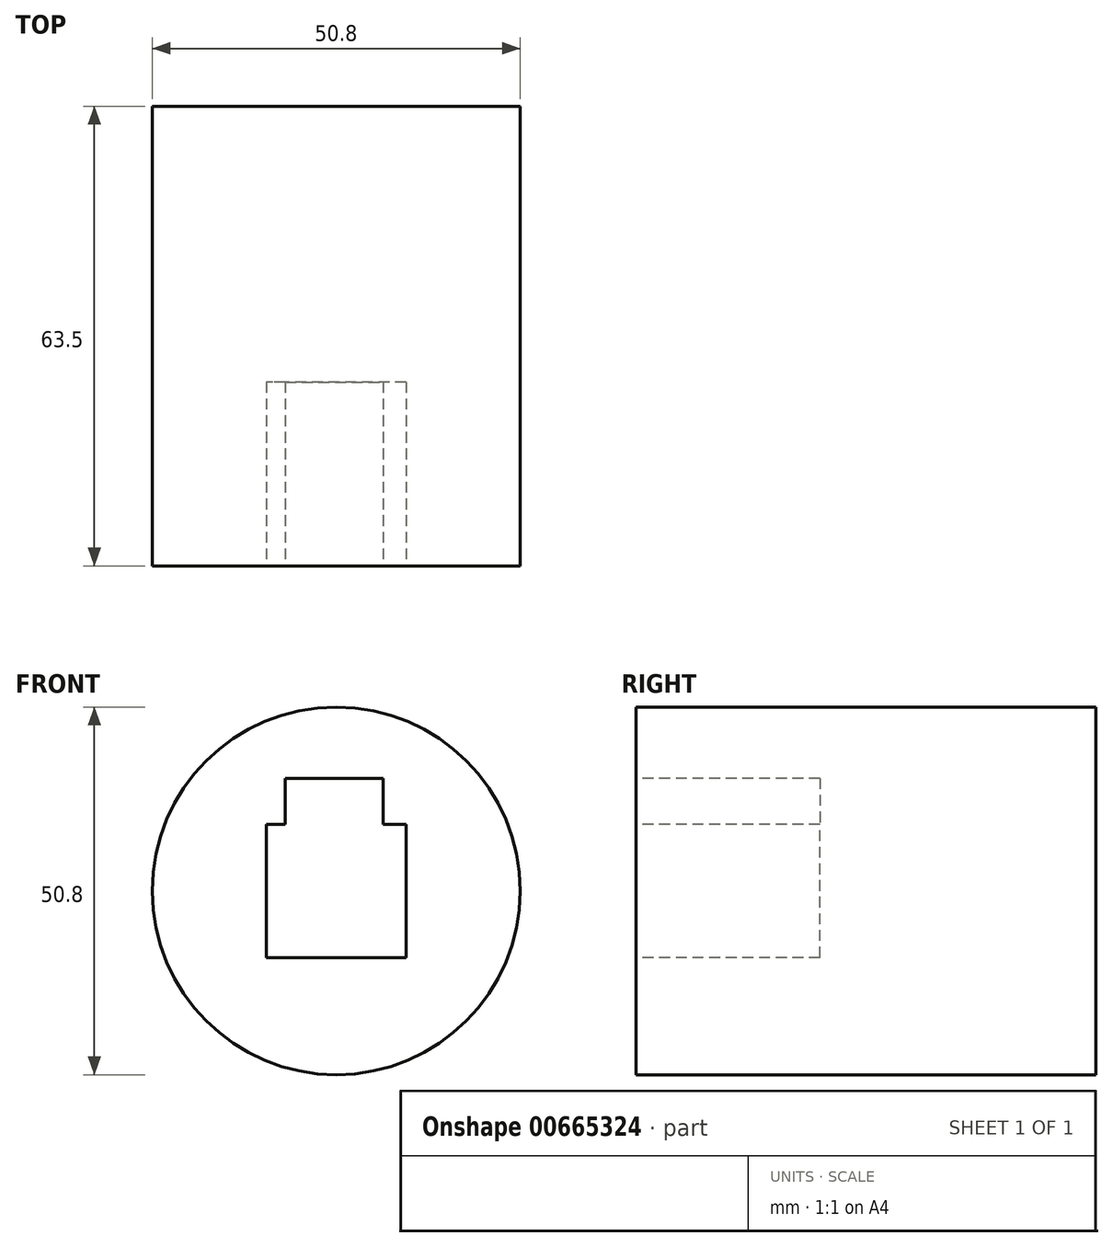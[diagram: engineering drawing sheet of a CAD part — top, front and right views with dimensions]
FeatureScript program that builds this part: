
annotation { "Feature Type Name" : "Feature", "Feature Type Description" : "" }
export const myFeature = defineFeature(function(context is Context, id is Id, definition is map)
    precondition{}
    {
        {
            var Q0;
            Q0=qCreatedBy(makeId("Front.planeOp"),FACE);
            var sketch = newSketch(context, id + "F0", { "sketchPlane" : qUnion([Q0])});
            skCircle(sketch, "E0", {"center": v(0, 0) * mm, "radius": 25.4 * mm});
            skSolve(sketch);
        }
        {
            var Q0;
            Q0 = qSketchRegion(id + "F0", true);
            extrude(context, id + "F1", {"entities" : qUnion([Q0]), "depth" : 63.5 * mm, "offsetDistance" : 25.4 * mm});
        }
        {
            var Q0;
            Q0=makeQuery(id+"F1.opExtrude","CAP_FACE",FACE,{"disambiguationData":[OSD([sQuery(id+"F0.wireOp",EDGE,"E0")])],"isStart":false});
            var sketch = newSketch(context, id + "F2", { "sketchPlane" : qUnion([Q0])});
            skLineSegment(sketch, "E1.bottom", {"start": v(9.64, -9.21) * mm, "end": v(-9.64, -9.21) * mm});
            skLineSegment(sketch, "E1.top", {"start": v(9.64, 9.21) * mm, "end": v(-9.64, 9.21) * mm});
            skLineSegment(sketch, "E1.left", {"start": v(9.64, -9.21) * mm, "end": v(9.64, 9.21) * mm});
            skLineSegment(sketch, "E1.right", {"start": v(-9.64, -9.21) * mm, "end": v(-9.64, 9.21) * mm});
            skPoint(sketch, "E1.middle", {"position": v(0, 0) * mm});
            skSolve(sketch);
        }
        {
            var Q0;
            Q0 = qSketchRegion(id + "F2", true);
            extrude(context, id + "F3", {"entities" : qUnion([Q0]), "operationType" : NewBodyOperationType.REMOVE, "oppositeDirection" : true, "depth" : 25.4 * mm, "offsetDistance" : 25.4 * mm});
        }
        {
            var Q0;
            Q0=makeQuery(id+"F1.opExtrude","CAP_FACE",FACE,{"disambiguationData":[OSD([sQuery(id+"F0.wireOp",EDGE,"E0")])],"isStart":false});
            var sketch = newSketch(context, id + "F4", { "sketchPlane" : qUnion([Q0])});
            skLineSegment(sketch, "E2.bottom", {"start": v(-7.05, 15.56) * mm, "end": v(6.46, 15.56) * mm});
            skLineSegment(sketch, "E2.top", {"start": v(-7.05, 6.3) * mm, "end": v(6.46, 6.3) * mm});
            skLineSegment(sketch, "E2.left", {"start": v(-7.05, 15.56) * mm, "end": v(-7.05, 6.3) * mm});
            skLineSegment(sketch, "E2.right", {"start": v(6.46, 15.56) * mm, "end": v(6.46, 6.3) * mm});
            skSolve(sketch);
        }
        {
            var Q0;
            Q0 = qSketchRegion(id + "F4", true);
            extrude(context, id + "F5", {"entities" : qUnion([Q0]), "operationType" : NewBodyOperationType.REMOVE, "oppositeDirection" : true, "depth" : 25.4 * mm, "offsetDistance" : 25.4 * mm});
        }
    });
